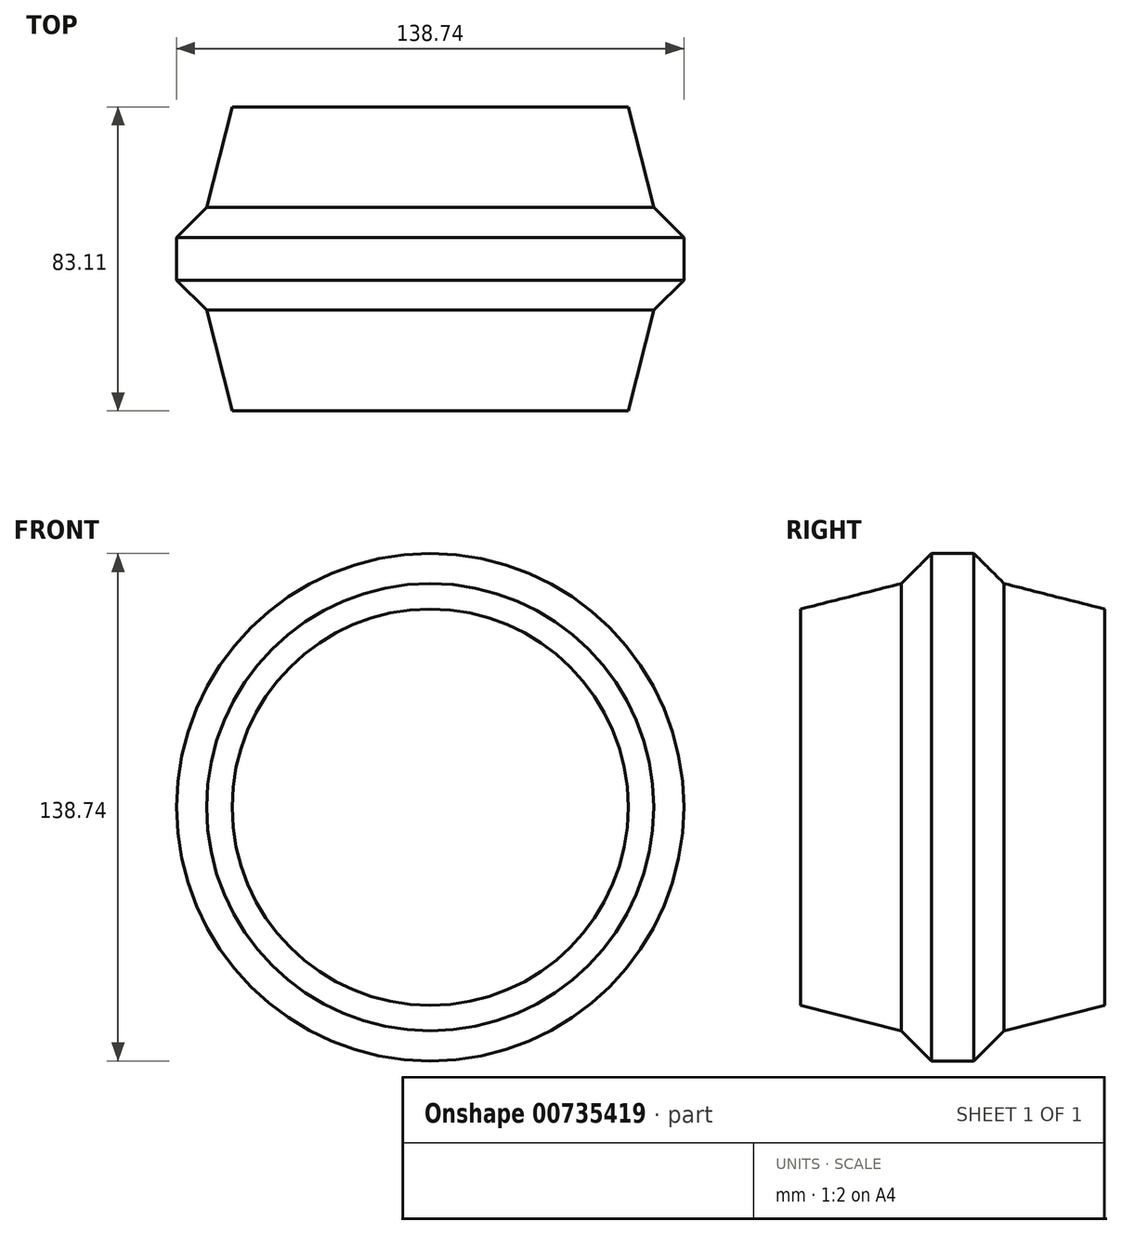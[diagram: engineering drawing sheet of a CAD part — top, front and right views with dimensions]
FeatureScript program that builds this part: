
annotation { "Feature Type Name" : "Feature", "Feature Type Description" : "" }
export const myFeature = defineFeature(function(context is Context, id is Id, definition is map)
    precondition{}
    {
        {
            var Q0;
            Q0=qCreatedBy(makeId("Top.planeOp"),FACE);
            var sketch = newSketch(context, id + "F0", { "sketchPlane" : qUnion([Q0])});
            skLineSegment(sketch, "E0", {"start": v(0, 0) * mm, "end": v(-54.18, 0) * mm});
            skLineSegment(sketch, "E1", {"start": v(-54.18, 0) * mm, "end": v(-59.81, -22.24) * mm});
            skLineSegment(sketch, "E2", {"start": v(0, 0) * mm, "end": v(0, -22.37) * mm});
            skLineSegment(sketch, "E3", {"start": v(-59.81, -22.24) * mm, "end": v(-61.15, -27.52) * mm});
            skLineSegment(sketch, "E4", {"start": v(-61.15, -27.52) * mm, "end": v(0, -27.52) * mm});
            skLineSegment(sketch, "E5", {"start": v(0, -27.52) * mm, "end": v(0, 0) * mm});
            skLineSegment(sketch, "E6", {"start": v(0, -47.98) * mm, "end": v(0, -27.52) * mm});
            skLineSegment(sketch, "E7", {"start": v(-61.15, -27.52) * mm, "end": v(-69.37, -35.74) * mm});
            skLineSegment(sketch, "E8", {"start": v(-69.37, -35.74) * mm, "end": v(-69.37, -47.37) * mm});
            skLineSegment(sketch, "E9", {"start": v(-69.37, -41.56) * mm, "end": v(45.82, -41.56) * mm});
            skLineSegment(sketch, "E10.MirrorCS", {"start": v(0, -83.11) * mm, "end": v(-54.18, -83.11) * mm});
            skLineSegment(sketch, "E11.MirrorCS", {"start": v(0, -55.6) * mm, "end": v(0, -83.11) * mm});
            skLineSegment(sketch, "E12.MirrorCS", {"start": v(-61.15, -55.6) * mm, "end": v(0, -55.6) * mm});
            skLineSegment(sketch, "E13.MirrorCS", {"start": v(-54.18, -83.11) * mm, "end": v(-59.81, -60.88) * mm});
            skLineSegment(sketch, "E14.MirrorCS", {"start": v(-59.81, -60.88) * mm, "end": v(-61.15, -55.6) * mm});
            skLineSegment(sketch, "E15.MirrorCS", {"start": v(-61.15, -55.6) * mm, "end": v(-69.37, -47.37) * mm});
            skLineSegment(sketch, "E16", {"start": v(0, -47.98) * mm, "end": v(0, -55.6) * mm});
            skSolve(sketch);
        }
        {
            var Q0;
            Q0=makeQuery(id+"F0.imprint","IMPRINT",FACE,{"disambiguationData":[TD([[makeQuery(id+"F0.imprint","IMPRINT",EDGE,{"derivedFrom":sQuery(id+"F0.wireOp",EDGE,"E0")}),1.0]])]});
            var Q1;
            Q1=makeQuery(id+"F0.imprint","IMPRINT",FACE,{"disambiguationData":[TD([[makeQuery(id+"F0.imprint","IMPRINT",EDGE,{"derivedFrom":sQuery(id+"F0.wireOp",EDGE,"E4")}),-1.0]])]});
            var Q2;
            Q2=makeQuery(id+"F0.imprint","IMPRINT",FACE,{"disambiguationData":[TD([[makeQuery(id+"F0.imprint","IMPRINT",EDGE,{"derivedFrom":sQuery(id+"F0.wireOp",EDGE,"E12.MirrorCS")}),1.0]])]});
            var Q3;
            Q3=makeQuery(id+"F0.imprint","IMPRINT",FACE,{"disambiguationData":[TD([[makeQuery(id+"F0.imprint","IMPRINT",EDGE,{"derivedFrom":sQuery(id+"F0.wireOp",EDGE,"E10.MirrorCS")}),-1.0]])]});
            var Q4;
            Q4=sQuery(id+"F0.wireOp",EDGE,"E2");
            revolve(context, id + "F1", {"surfaceOperationType" : NewSurfaceOperationType.NEW, "entities" : qUnion([Q0, Q1, Q2, Q3]), "axis" : qUnion([Q4]), "revolveType" : RevolveType.FULL});
        }
    });
